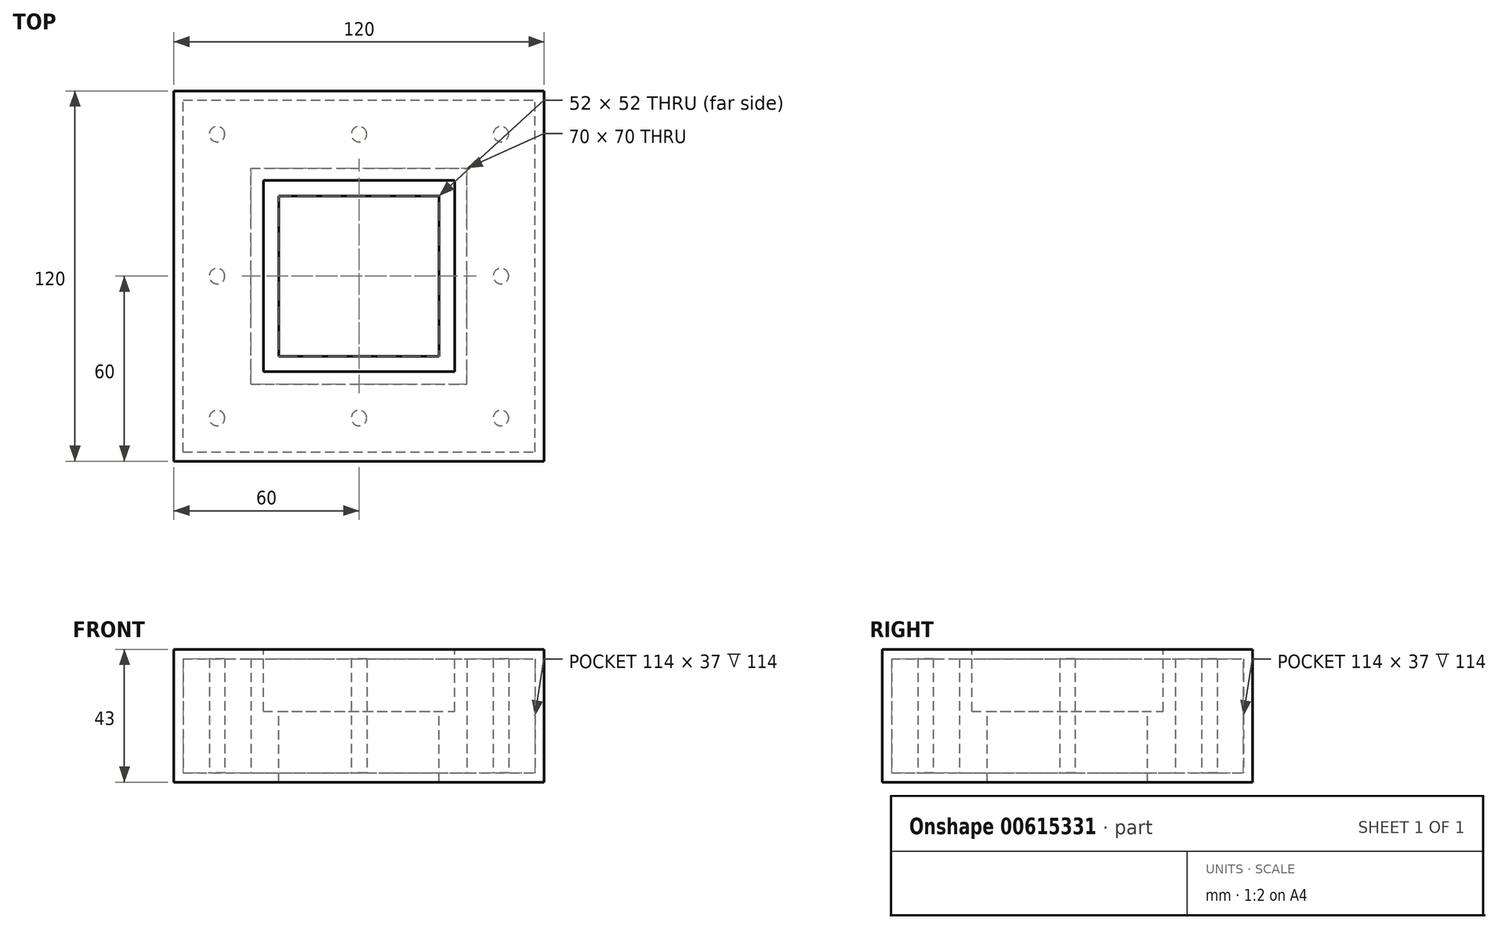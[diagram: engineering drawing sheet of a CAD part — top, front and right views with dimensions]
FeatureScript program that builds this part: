
annotation { "Feature Type Name" : "Feature", "Feature Type Description" : "" }
export const myFeature = defineFeature(function(context is Context, id is Id, definition is map)
    precondition{}
    {
        {
            var Q0;
            Q0=qCreatedBy(makeId("Top.planeOp"),FACE);
            var sketch = newSketch(context, id + "F0", { "sketchPlane" : qUnion([Q0])});
            skLineSegment(sketch, "E0.bottom", {"start": v(-60, -60) * mm, "end": v(60, -60) * mm});
            skLineSegment(sketch, "E0.top", {"start": v(-60, 60) * mm, "end": v(60, 60) * mm});
            skLineSegment(sketch, "E0.left", {"start": v(-60, -60) * mm, "end": v(-60, 60) * mm});
            skLineSegment(sketch, "E0.right", {"start": v(60, -60) * mm, "end": v(60, 60) * mm});
            skPoint(sketch, "E0.middle", {"position": v(0, 0) * mm});
            skSolve(sketch);
        }
        {
            var Q0;
            Q0=qSketchRegion(id+"F0",true);
            extrude(context, id + "F1", {"entities" : qUnion([Q0]), "depth" : 3 * mm, "offsetDistance" : 25 * mm});
        }
        {
            var Q0;
            Q0=makeQuery(id+"F1.opExtrude","CAP_FACE",FACE,{"disambiguationData":[OSD([sQuery(id+"F0.wireOp",EDGE,"E0.bottom"),sQuery(id+"F0.wireOp",EDGE,"E0.top"),sQuery(id+"F0.wireOp",EDGE,"E0.left"),sQuery(id+"F0.wireOp",EDGE,"E0.right")])],"isStart":false});
            var sketch = newSketch(context, id + "F2", { "sketchPlane" : qUnion([Q0])});
            skLineSegment(sketch, "E1.bottom", {"start": v(-26, -26) * mm, "end": v(26, -26) * mm});
            skLineSegment(sketch, "E1.top", {"start": v(-26, 26) * mm, "end": v(26, 26) * mm});
            skLineSegment(sketch, "E1.left", {"start": v(-26, -26) * mm, "end": v(-26, 26) * mm});
            skLineSegment(sketch, "E1.right", {"start": v(26, -26) * mm, "end": v(26, 26) * mm});
            skPoint(sketch, "E1.middle", {"position": v(0, 0) * mm});
            skLineSegment(sketch, "E2.bottom", {"start": v(-35, -35) * mm, "end": v(35, -35) * mm});
            skLineSegment(sketch, "E2.top", {"start": v(-35, 35) * mm, "end": v(35, 35) * mm});
            skLineSegment(sketch, "E2.left", {"start": v(-35, -35) * mm, "end": v(-35, 35) * mm});
            skLineSegment(sketch, "E2.right", {"start": v(35, -35) * mm, "end": v(35, 35) * mm});
            skLineSegment(sketch, "E3.bottom", {"start": v(-57, -57) * mm, "end": v(57, -57) * mm});
            skLineSegment(sketch, "E3.top", {"start": v(-57, 57) * mm, "end": v(57, 57) * mm});
            skLineSegment(sketch, "E3.left", {"start": v(-57, -57) * mm, "end": v(-57, 57) * mm});
            skLineSegment(sketch, "E3.right", {"start": v(57, -57) * mm, "end": v(57, 57) * mm});
            skLineSegment(sketch, "E4", {"start": v(-57, 35) * mm, "end": v(-57, 57) * mm});
            skLineSegment(sketch, "E5", {"start": v(-35, 57) * mm, "end": v(-57, 57) * mm});
            skLineSegment(sketch, "E6", {"start": v(35, 35) * mm, "end": v(57, 35) * mm});
            skLineSegment(sketch, "E7", {"start": v(57, 35) * mm, "end": v(57, 57) * mm});
            skLineSegment(sketch, "E8", {"start": v(35, 57) * mm, "end": v(57, 57) * mm});
            skLineSegment(sketch, "E9", {"start": v(35, -35) * mm, "end": v(57, -35) * mm});
            skLineSegment(sketch, "E10", {"start": v(57, -35) * mm, "end": v(57, -57) * mm});
            skLineSegment(sketch, "E11", {"start": v(57, -57) * mm, "end": v(35, -57) * mm});
            skLineSegment(sketch, "E12", {"start": v(-35, -35) * mm, "end": v(-57, -35) * mm});
            skLineSegment(sketch, "E13", {"start": v(-57, -35) * mm, "end": v(-57, -57) * mm});
            skLineSegment(sketch, "E14", {"start": v(-57, -57) * mm, "end": v(-35, -57) * mm});
            skPoint(sketch, "E15", {"position": v(-46, 46) * mm});
            skPoint(sketch, "E15.positionSnap0", {"position": v(-57, 46) * mm});
            skPoint(sketch, "E15.positionSnap1", {"position": v(-46, 57) * mm});
            skPoint(sketch, "E16", {"position": v(46, 46) * mm});
            skPoint(sketch, "E16.positionSnap0", {"position": v(57, 46) * mm});
            skPoint(sketch, "E16.positionSnap1", {"position": v(46, 57) * mm});
            skPoint(sketch, "E17", {"position": v(46, -46) * mm});
            skPoint(sketch, "E17.positionSnap0", {"position": v(57, -46) * mm});
            skPoint(sketch, "E17.positionSnap1", {"position": v(46, 35) * mm});
            skPoint(sketch, "E18", {"position": v(-46, -46) * mm});
            skPoint(sketch, "E18.positionSnap0", {"position": v(-46, -57) * mm});
            skPoint(sketch, "E18.positionSnap1", {"position": v(-57, -46) * mm});
            skPoint(sketch, "E19", {"position": v(0, -46) * mm});
            skPoint(sketch, "E19.positionSnap0", {"position": v(0, -57) * mm});
            skPoint(sketch, "E20", {"position": v(0, 46) * mm});
            skPoint(sketch, "E20.positionSnap0", {"position": v(0, 57) * mm});
            skCircle(sketch, "E21", {"center": v(-46, 46) * mm, "radius": 2.5 * mm});
            skCircle(sketch, "E22", {"center": v(0, 46) * mm, "radius": 2.5 * mm});
            skCircle(sketch, "E23", {"center": v(46, 46) * mm, "radius": 2.5 * mm});
            skCircle(sketch, "E24", {"center": v(46, -46) * mm, "radius": 2.5 * mm});
            skCircle(sketch, "E25", {"center": v(0, -46) * mm, "radius": 2.5 * mm});
            skCircle(sketch, "E26", {"center": v(-46, -46) * mm, "radius": 2.5 * mm});
            skCircle(sketch, "E27", {"center": v(46, 0) * mm, "radius": 2.5 * mm});
            skCircle(sketch, "E28", {"center": v(-46, 0) * mm, "radius": 2.5 * mm});
            skSolve(sketch);
        }
        {
            var Q0;
            Q0=makeQuery(id+"F2.imprint","IMPRINT",FACE,{"disambiguationData":[TD([[makeQuery(id+"F2.imprint","IMPRINT",EDGE,{"derivedFrom":sQuery(id+"F2.wireOp",EDGE,"E1.bottom")}),1.0]])]});
            extrude(context, id + "F3", {"entities" : qUnion([Q0]), "operationType" : NewBodyOperationType.REMOVE, "oppositeDirection" : true, "depth" : 25 * mm, "offsetDistance" : 25 * mm});
        }
        {
            var Q0;
            Q0=makeQuery(id+"F2.imprint","IMPRINT",FACE,{"disambiguationData":[TD([[makeQuery(id+"F2.imprint","IMPRINT",EDGE,{"derivedFrom":sQuery(id+"F2.wireOp",EDGE,"E23")}),1.0]])]});
            var Q1;
            Q1=makeQuery(id+"F2.imprint","IMPRINT",FACE,{"disambiguationData":[TD([[makeQuery(id+"F2.imprint","IMPRINT",EDGE,{"derivedFrom":sQuery(id+"F2.wireOp",EDGE,"E22")}),1.0]])]});
            var Q2;
            Q2=makeQuery(id+"F2.imprint","IMPRINT",FACE,{"disambiguationData":[TD([[makeQuery(id+"F2.imprint","IMPRINT",EDGE,{"derivedFrom":sQuery(id+"F2.wireOp",EDGE,"E21")}),1.0]])]});
            var Q3;
            Q3=makeQuery(id+"F2.imprint","IMPRINT",FACE,{"disambiguationData":[TD([[makeQuery(id+"F2.imprint","IMPRINT",EDGE,{"derivedFrom":sQuery(id+"F2.wireOp",EDGE,"E28")}),1.0]])]});
            var Q4;
            Q4=makeQuery(id+"F2.imprint","IMPRINT",FACE,{"disambiguationData":[TD([[makeQuery(id+"F2.imprint","IMPRINT",EDGE,{"derivedFrom":sQuery(id+"F2.wireOp",EDGE,"E26")}),1.0]])]});
            var Q5;
            Q5=makeQuery(id+"F2.imprint","IMPRINT",FACE,{"disambiguationData":[TD([[makeQuery(id+"F2.imprint","IMPRINT",EDGE,{"derivedFrom":sQuery(id+"F2.wireOp",EDGE,"E25")}),1.0]])]});
            var Q6;
            Q6=makeQuery(id+"F2.imprint","IMPRINT",FACE,{"disambiguationData":[TD([[makeQuery(id+"F2.imprint","IMPRINT",EDGE,{"derivedFrom":sQuery(id+"F2.wireOp",EDGE,"E24")}),1.0]])]});
            var Q7;
            Q7=makeQuery(id+"F2.imprint","IMPRINT",FACE,{"disambiguationData":[TD([[makeQuery(id+"F2.imprint","IMPRINT",EDGE,{"derivedFrom":sQuery(id+"F2.wireOp",EDGE,"E27")}),1.0]])]});
            var Q8;
            Q8=makeQuery(id+"F2.imprint","IMPRINT",FACE,{"disambiguationData":[TD([[makeQuery(id+"F2.imprint","IMPRINT",EDGE,{"derivedFrom":sQuery(id+"F2.wireOp",EDGE,"E3.bottom")}),-1.0]])]});
            var Q9;
            Q9=makeQuery(id+"F2.imprint","IMPRINT",FACE,{"disambiguationData":[TD([[makeQuery(id+"F2.imprint","IMPRINT",EDGE,{"derivedFrom":sQuery(id+"F2.wireOp",EDGE,"E1.bottom")}),-1.0]])]});
            extrude(context, id + "F4", {"entities" : qUnion([Q0, Q1, Q2, Q3, Q4, Q5, Q6, Q7, Q8, Q9]), "operationType" : NewBodyOperationType.ADD, "depth" : 37 * mm, "offsetDistance" : 25 * mm});
        }
        {
            var Q0;
            Q0=makeQuery(id+"F4.opExtrude","CAP_FACE",FACE,{"disambiguationData":[OSD([sQuery(id+"F0.wireOp",EDGE,"E0.bottom"),sQuery(id+"F0.wireOp",EDGE,"E0.top"),sQuery(id+"F0.wireOp",EDGE,"E0.left"),sQuery(id+"F0.wireOp",EDGE,"E0.right"),sQuery(id+"F2.wireOp",EDGE,"E3.bottom"),sQuery(id+"F2.wireOp",EDGE,"E3.top"),sQuery(id+"F2.wireOp",EDGE,"E3.left"),sQuery(id+"F2.wireOp",EDGE,"E3.right"),sQuery(id+"F2.wireOp",EDGE,"E4"),sQuery(id+"F2.wireOp",EDGE,"E7"),sQuery(id+"F2.wireOp",EDGE,"E8"),sQuery(id+"F2.wireOp",EDGE,"E5"),sQuery(id+"F2.wireOp",EDGE,"E10"),sQuery(id+"F2.wireOp",EDGE,"E11"),sQuery(id+"F2.wireOp",EDGE,"E13"),sQuery(id+"F2.wireOp",EDGE,"E14")])],"isStart":false});
            var sketch = newSketch(context, id + "F5", { "sketchPlane" : qUnion([Q0])});
            skPoint(sketch, "E29.middle", {"position": v(0, 0) * mm});
            skLineSegment(sketch, "E30", {"start": v(-60, 60) * mm, "end": v(-60, -60) * mm});
            skLineSegment(sketch, "E31", {"start": v(-60, -60) * mm, "end": v(60, -60) * mm});
            skLineSegment(sketch, "E32", {"start": v(60, -60) * mm, "end": v(60, 60) * mm});
            skLineSegment(sketch, "E33", {"start": v(60, 60) * mm, "end": v(-60, 60) * mm});
            skLineSegment(sketch, "E34.bottom", {"start": v(-26, -26) * mm, "end": v(26, -26) * mm});
            skLineSegment(sketch, "E34.top", {"start": v(-26, 26) * mm, "end": v(26, 26) * mm});
            skLineSegment(sketch, "E34.left", {"start": v(-26, -26) * mm, "end": v(-26, 26) * mm});
            skLineSegment(sketch, "E34.right", {"start": v(26, -26) * mm, "end": v(26, 26) * mm});
            skSolve(sketch);
        }
        {
            var Q0;
            Q0=makeQuery(id+"F5.imprint","IMPRINT",FACE,{"disambiguationData":[TD([[makeQuery(id+"F5.imprint","IMPRINT",EDGE,{"derivedFrom":sQuery(id+"F5.wireOp",EDGE,"E34.bottom")}),-1.0]])]});
            var Q1;
            Q1=makeQuery(id+"F5.imprint","IMPRINT",FACE,{"disambiguationData":[TD([[makeQuery(id+"F5.imprint","IMPRINT",EDGE,{"derivedFrom":sQuery(id+"F5.wireOp",EDGE,"E30")}),-1.0]])]});
            extrude(context, id + "F6", {"entities" : qUnion([Q0, Q1]), "operationType" : NewBodyOperationType.ADD, "depth" : 3 * mm, "offsetDistance" : 25 * mm});
        }
        {
            var Q0;
            Q0=makeQuery(id+"F6.opExtrude","CAP_FACE",FACE,{"disambiguationData":[OSD([sQuery(id+"F5.wireOp",EDGE,"E30"),sQuery(id+"F5.wireOp",EDGE,"E31"),sQuery(id+"F5.wireOp",EDGE,"E32"),sQuery(id+"F5.wireOp",EDGE,"E33"),sQuery(id+"F5.wireOp",EDGE,"E34.bottom"),sQuery(id+"F5.wireOp",EDGE,"E34.top"),sQuery(id+"F5.wireOp",EDGE,"E34.left"),sQuery(id+"F5.wireOp",EDGE,"E34.right")])],"isStart":false});
            var sketch = newSketch(context, id + "F7", { "sketchPlane" : qUnion([Q0])});
            skLineSegment(sketch, "E35.bottom", {"start": v(-31, -31) * mm, "end": v(31, -31) * mm});
            skLineSegment(sketch, "E35.top", {"start": v(-31, 31) * mm, "end": v(31, 31) * mm});
            skLineSegment(sketch, "E35.left", {"start": v(-31, -31) * mm, "end": v(-31, 31) * mm});
            skLineSegment(sketch, "E35.right", {"start": v(31, -31) * mm, "end": v(31, 31) * mm});
            skPoint(sketch, "E35.middle", {"position": v(0, 0) * mm});
            skLineSegment(sketch, "E36.bottom", {"start": v(-26, -26) * mm, "end": v(26, -26) * mm});
            skLineSegment(sketch, "E36.top", {"start": v(-26, 26) * mm, "end": v(26, 26) * mm});
            skLineSegment(sketch, "E36.left", {"start": v(-26, -26) * mm, "end": v(-26, 26) * mm});
            skLineSegment(sketch, "E36.right", {"start": v(26, -26) * mm, "end": v(26, 26) * mm});
            skSolve(sketch);
        }
        {
            var Q0;
            Q0=makeQuery(id+"F7.imprint","IMPRINT",FACE,{"disambiguationData":[TD([[makeQuery(id+"F7.imprint","IMPRINT",EDGE,{"derivedFrom":sQuery(id+"F7.wireOp",EDGE,"E35.bottom")}),1.0]])]});
            extrude(context, id + "F8", {"entities" : qUnion([Q0]), "operationType" : NewBodyOperationType.REMOVE, "oppositeDirection" : true, "depth" : 20 * mm, "offsetDistance" : 25 * mm});
        }
    });
